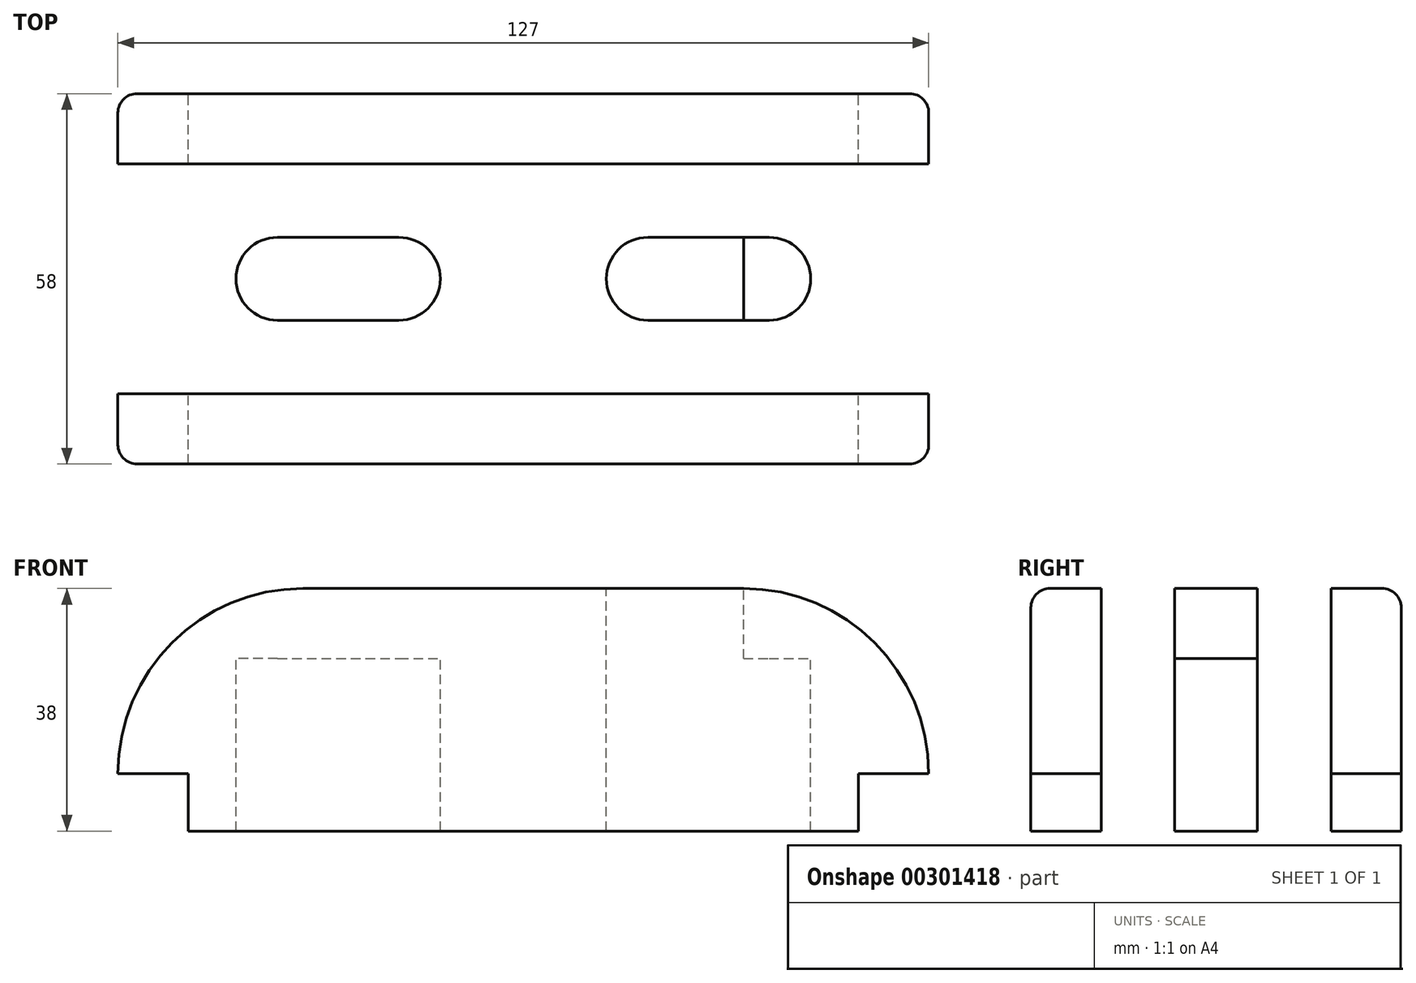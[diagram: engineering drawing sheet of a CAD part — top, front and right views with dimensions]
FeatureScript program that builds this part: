
annotation { "Feature Type Name" : "Feature", "Feature Type Description" : "" }
export const myFeature = defineFeature(function(context is Context, id is Id, definition is map)
    precondition{}
    {
        {
            var Q0;
            Q0=qCreatedBy(makeId("Front.planeOp"),FACE);
            var sketch = newSketch(context, id + "F0", { "sketchPlane" : qUnion([Q0])});
            skLineSegment(sketch, "E0.bottom", {"start": v(-34.5, 38) * mm, "end": v(34.5, 38) * mm});
            skLineSegment(sketch, "E0.top", {"start": v(-52.5, 0) * mm, "end": v(52.5, 0) * mm});
            skArc(sketch, "E1", {"start": v(-34.5, 38) * mm, "mid": v(-55, 29.5) * mm, "end": v(-63.5, 9) * mm});
            skArc(sketch, "E2", {"start": v(63.5, 9) * mm, "mid": v(55, 29.5) * mm, "end": v(34.5, 38) * mm});
            skLineSegment(sketch, "E3.bottom", {"start": v(-63.5, 9) * mm, "end": v(-52.5, 9) * mm});
            skLineSegment(sketch, "E3.right", {"start": v(-52.5, 9) * mm, "end": v(-52.5, 0) * mm});
            skLineSegment(sketch, "E4.top", {"start": v(52.5, 9) * mm, "end": v(63.5, 9) * mm});
            skLineSegment(sketch, "E4.left", {"start": v(52.5, 0) * mm, "end": v(52.5, 9) * mm});
            skSolve(sketch);
        }
        {
            var Q0;
            Q0=makeQuery(id+"F0.imprint","IMPRINT",FACE,{"disambiguationData":[TD([[makeQuery(id+"F0.imprint","IMPRINT",EDGE,{"derivedFrom":sQuery(id+"F0.wireOp",EDGE,"E0.bottom")}),-1.0]])]});
            extrude(context, id + "F1", {"entities" : qUnion([Q0]), "endBound" : BoundingType.SYMMETRIC, "depth" : 58 * mm});
        }
        {
            var Q0;
            Q0=makeQuery(id+"F1.opExtrude","SWEPT_FACE",FACE,{"disambiguationData":[OSD([sQuery(id+"F0.wireOp",EDGE,"E0.bottom")])]});
            var sketch = newSketch(context, id + "F2", { "sketchPlane" : qUnion([Q0])});
            skLineSegment(sketch, "E5", {"start": v(-38.5, 0) * mm, "end": v(-19.5, 0) * mm, "construction": true});
            skPoint(sketch, "E5.startSnap0", {"position": v(-34.5, 0) * mm});
            skPoint(sketch, "E5.endSnap0", {"position": v(-34.5, 0) * mm});
            skLineSegment(sketch, "E6", {"start": v(19.5, 0) * mm, "end": v(38.5, 0) * mm, "construction": true});
            skPoint(sketch, "E6.endSnap0", {"position": v(34.5, 0) * mm});
            skArc(sketch, "E7.0.startCap", {"start": v(-38.5, -6.5) * mm, "mid": v(-45, 0) * mm, "end": v(-38.5, 6.5) * mm});
            skArc(sketch, "E7.0.endCap", {"start": v(-19.5, 6.5) * mm, "mid": v(-13, 0) * mm, "end": v(-19.5, -6.5) * mm});
            skLineSegment(sketch, "E7.0.left", {"start": v(-38.5, 6.5) * mm, "end": v(-19.5, 6.5) * mm});
            skLineSegment(sketch, "E7.0.right", {"start": v(-38.5, -6.5) * mm, "end": v(-19.5, -6.5) * mm});
            skArc(sketch, "E7.1.startCap", {"start": v(19.5, -6.5) * mm, "mid": v(13, 0) * mm, "end": v(19.5, 6.5) * mm});
            skArc(sketch, "E7.1.endCap", {"start": v(38.5, 6.5) * mm, "mid": v(45, 0) * mm, "end": v(38.5, -6.5) * mm});
            skLineSegment(sketch, "E7.1.left", {"start": v(19.5, 6.5) * mm, "end": v(38.5, 6.5) * mm});
            skLineSegment(sketch, "E7.1.right", {"start": v(19.5, -6.5) * mm, "end": v(38.5, -6.5) * mm});
            skLineSegment(sketch, "E8.0", {"start": v(-34.5, 29) * mm, "end": v(-63.5, 29) * mm});
            skLineSegment(sketch, "E9.0", {"start": v(-34.5, 29) * mm, "end": v(34.5, 29) * mm});
            skLineSegment(sketch, "E10.0", {"start": v(63.5, 29) * mm, "end": v(34.5, 29) * mm});
            skLineSegment(sketch, "E11.0", {"start": v(-63.5, -29) * mm, "end": v(-63.5, 29) * mm});
            skLineSegment(sketch, "E12.0", {"start": v(-34.5, -29) * mm, "end": v(-63.5, -29) * mm});
            skLineSegment(sketch, "E13.0", {"start": v(-34.5, -29) * mm, "end": v(34.5, -29) * mm});
            skLineSegment(sketch, "E14.0", {"start": v(63.5, -29) * mm, "end": v(34.5, -29) * mm});
            skLineSegment(sketch, "E15.0", {"start": v(63.5, -29) * mm, "end": v(63.5, 29) * mm});
            skLineSegment(sketch, "E16.bottom", {"start": v(-63.5, 18) * mm, "end": v(63.5, 18) * mm});
            skLineSegment(sketch, "E16.top", {"start": v(-63.5, -18) * mm, "end": v(63.5, -18) * mm});
            skLineSegment(sketch, "E16.left", {"start": v(-63.5, 18) * mm, "end": v(-63.5, -18) * mm});
            skLineSegment(sketch, "E16.right", {"start": v(63.5, 18) * mm, "end": v(63.5, -18) * mm});
            skLineSegment(sketch, "E17", {"start": v(-75.55, 0) * mm, "end": v(92.55, 0) * mm, "construction": true});
            skPoint(sketch, "E17.startSnap0", {"position": v(-13, 0) * mm});
            skPoint(sketch, "E17.endSnap0", {"position": v(63.5, 0) * mm});
            skSolve(sketch);
        }
        {
            var Q0;
            {var subQ0=sQuery(id+"F2.wireOp",EDGE,"E7.0.startCap");Q0=makeQuery(id+"F2.imprint","IMPRINT",FACE,{"disambiguationData":[TD([[makeQuery(id+"F2.imprint","IMPRINT",EDGE,{"derivedFrom":subQ0}),-1.0]])]});}
            var Q1;
            {var subQ0=sQuery(id+"F2.wireOp",EDGE,"E7.0.endCap");Q1=makeQuery(id+"F2.imprint","IMPRINT",FACE,{"disambiguationData":[TD([[makeQuery(id+"F2.imprint","IMPRINT",EDGE,{"derivedFrom":subQ0}),-1.0]])]});}
            var Q2;
            {var subQ0=sQuery(id+"F2.wireOp",EDGE,"E7.1.startCap");Q2=makeQuery(id+"F2.imprint","IMPRINT",FACE,{"disambiguationData":[TD([[makeQuery(id+"F2.imprint","IMPRINT",EDGE,{"derivedFrom":subQ0}),-1.0]])]});}
            var Q3;
            {var subQ0=sQuery(id+"F2.wireOp",EDGE,"E7.1.endCap");Q3=makeQuery(id+"F2.imprint","IMPRINT",FACE,{"disambiguationData":[TD([[makeQuery(id+"F2.imprint","IMPRINT",EDGE,{"derivedFrom":subQ0}),-1.0]])]});}
            extrude(context, id + "F3", {"entities" : qUnion([Q0, Q1, Q2, Q3]), "operationType" : NewBodyOperationType.REMOVE, "endBound" : BoundingType.THROUGH_ALL, "oppositeDirection" : true, "depth" : 25 * mm});
        }
        {
            var Q0;
            {var subQ1=sQuery(id+"F2.wireOp",EDGE,"E7.0.startCap");Q0=makeQuery(id+"F2.imprint","IMPRINT",FACE,{"disambiguationData":[TD([[makeQuery(id+"F2.imprint","IMPRINT",EDGE,{"derivedFrom":subQ1}),1.0]])]});}
            var Q1;
            {var subQ10=sQuery(id+"F2.wireOp",EDGE,"E7.0.endCap");Q1=makeQuery(id+"F2.imprint","IMPRINT",FACE,{"disambiguationData":[TD([[makeQuery(id+"F2.imprint","IMPRINT",EDGE,{"derivedFrom":subQ10}),1.0]])]});}
            var Q2;
            {var subQ1=sQuery(id+"F2.wireOp",EDGE,"E7.1.endCap");Q2=makeQuery(id+"F2.imprint","IMPRINT",FACE,{"disambiguationData":[TD([[makeQuery(id+"F2.imprint","IMPRINT",EDGE,{"derivedFrom":subQ1}),1.0]])]});}
            extrude(context, id + "F4", {"entities" : qUnion([Q0, Q1, Q2]), "operationType" : NewBodyOperationType.REMOVE, "oppositeDirection" : true, "depth" : 11 * mm});
        }
        {
            var Q0;
            Q0=makeQuery(id+"F1.opExtrude","CAP_EDGE",EDGE,{"disambiguationData":[OSD([sQuery(id+"F0.wireOp",EDGE,"E0.bottom")])],"isStart":false});
            var Q1;
            Q1=makeQuery(id+"F1.opExtrude","CAP_EDGE",EDGE,{"disambiguationData":[OSD([sQuery(id+"F0.wireOp",EDGE,"E0.bottom")])],"isStart":true});
            fillet(context, id + "F5", {"entities" : qUnion([Q0, Q1]), "radius" : 3 * mm, "tangentPropagation" : true, "allowEdgeOverflow" : false});
        }
    });
